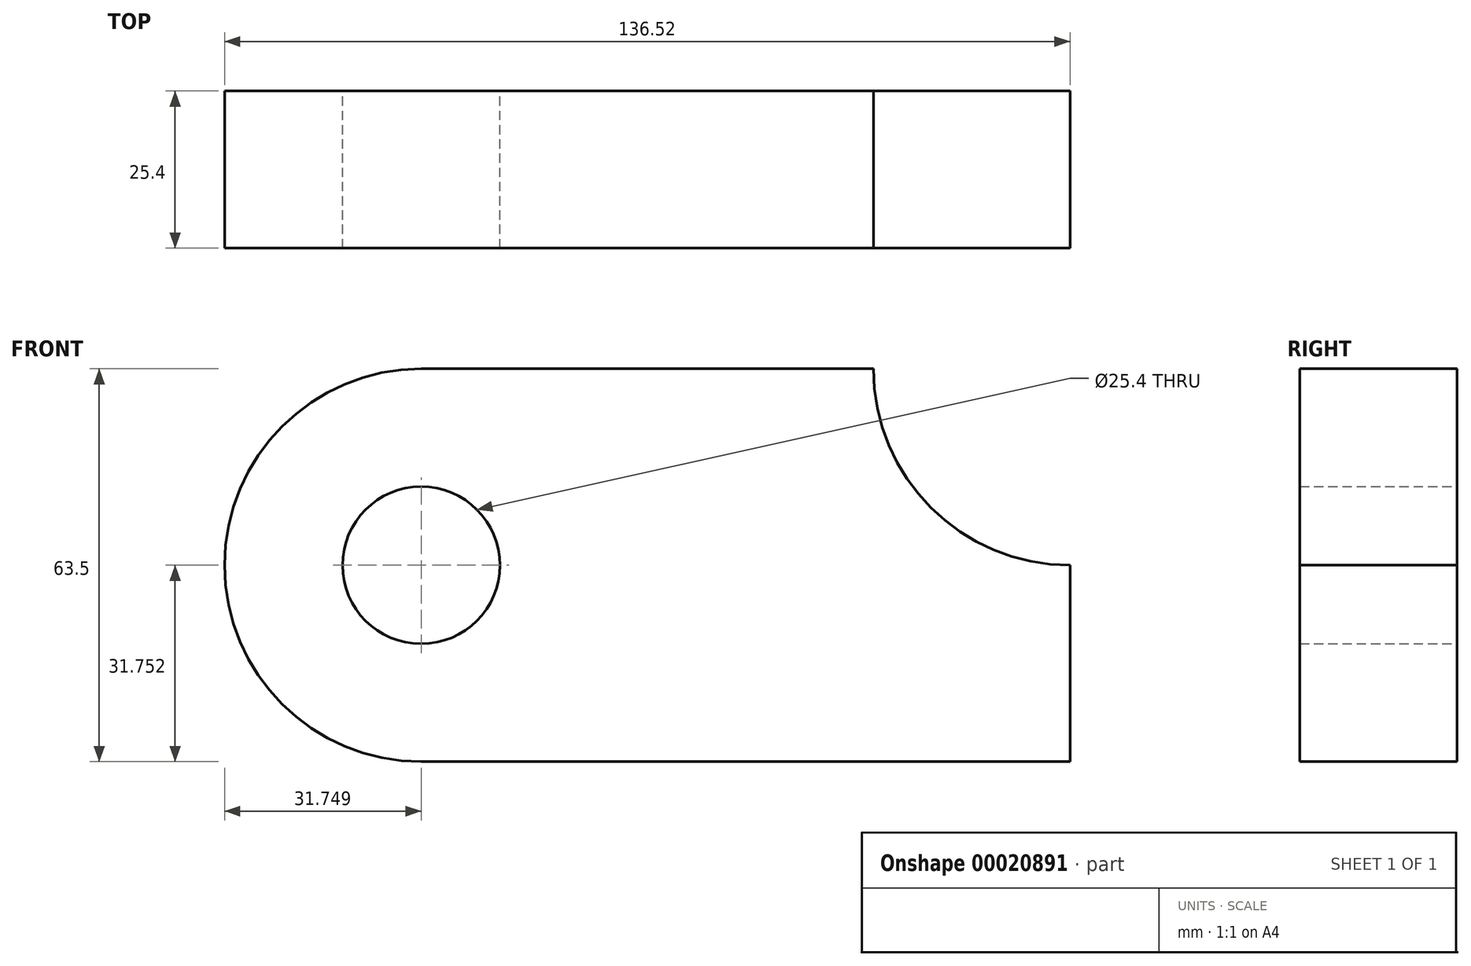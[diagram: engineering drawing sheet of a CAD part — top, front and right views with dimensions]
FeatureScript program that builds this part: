
annotation { "Feature Type Name" : "Feature", "Feature Type Description" : "" }
export const myFeature = defineFeature(function(context is Context, id is Id, definition is map)
    precondition{}
    {
        {
            var Q0;
            Q0=qCreatedBy(makeId("Front.planeOp"),FACE);
            var sketch = newSketch(context, id + "F0", { "sketchPlane" : qUnion([Q0])});
            skLineSegment(sketch, "E0.bottom", {"start": v(169.82, -14.82) * mm, "end": v(242.84, -14.82) * mm});
            skLineSegment(sketch, "E0.top", {"start": v(169.82, -78.32) * mm, "end": v(274.6, -78.32) * mm});
            skLineSegment(sketch, "E0.left", {"start": v(169.82, -14.82) * mm, "end": v(169.82, -78.32) * mm});
            skLineSegment(sketch, "E0.right", {"start": v(274.6, -46.57) * mm, "end": v(274.6, -78.32) * mm});
            skCircle(sketch, "E1", {"center": v(169.82, -46.57) * mm, "radius": 31.75 * mm});
            skCircle(sketch, "E2", {"center": v(169.82, -46.57) * mm, "radius": 12.7 * mm});
            skArc(sketch, "E3", {"start": v(242.84, -14.82) * mm, "mid": v(252.14, -37.27) * mm, "end": v(274.6, -46.57) * mm});
            skSolve(sketch);
        }
        {
            var Q0;
            Q0 = qSketchRegion(id + "F0", true);
            extrude(context, id + "F1", {"entities" : qUnion([Q0]), "depth" : 25.4 * mm});
        }
    });
